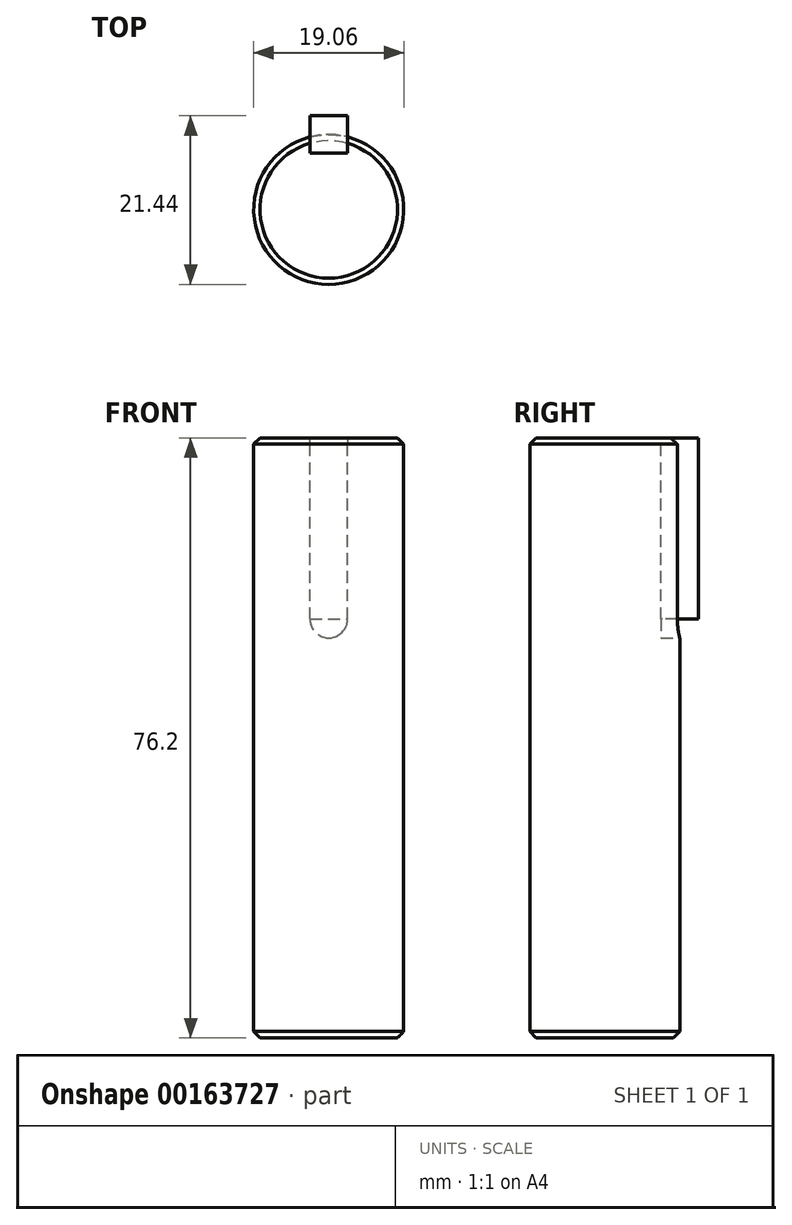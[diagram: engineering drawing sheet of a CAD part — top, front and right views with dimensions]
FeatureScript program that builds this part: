
annotation { "Feature Type Name" : "Feature", "Feature Type Description" : "" }
export const myFeature = defineFeature(function(context is Context, id is Id, definition is map)
    precondition{}
    {
        {
            var Q0;
            Q0=qCreatedBy(makeId("Top.planeOp"),FACE);
            var sketch = newSketch(context, id + "F0", { "sketchPlane" : qUnion([Q0])});
            skCircle(sketch, "E0", {"center": v(0, 0) * mm, "radius": 9.53 * mm});
            skSolve(sketch);
        }
        {
            var Q0;
            Q0=makeQuery(id+"F0.imprint","IMPRINT",FACE,{"disambiguationData":[TD([[makeQuery(id+"F0.imprint","IMPRINT",EDGE,{"derivedFrom":sQuery(id+"F0.wireOp",EDGE,"E0")}),1.0]])]});
            extrude(context, id + "F1", {"entities" : qUnion([Q0]), "depth" : 76.2 * mm});
        }
        {
            var Q0;
            Q0=makeQuery(id+"F1.opExtrude","CAP_FACE",FACE,{"disambiguationData":[OSD([sQuery(id+"F0.wireOp",EDGE,"E0")])],"isStart":false});
            var sketch = newSketch(context, id + "F2", { "sketchPlane" : qUnion([Q0])});
            skLineSegment(sketch, "E1.bottom", {"start": v(-2.38, 11.9) * mm, "end": v(2.38, 11.9) * mm});
            skLineSegment(sketch, "E1.top", {"start": v(-2.38, 7.14) * mm, "end": v(2.38, 7.14) * mm});
            skLineSegment(sketch, "E1.left", {"start": v(-2.38, 11.9) * mm, "end": v(-2.38, 7.14) * mm});
            skLineSegment(sketch, "E1.right", {"start": v(2.38, 11.9) * mm, "end": v(2.38, 7.14) * mm});
            skPoint(sketch, "E1.middle", {"position": v(0, 9.53) * mm});
            skSolve(sketch);
        }
        {
            var Q0;
            {var subQ0=sQuery(id+"F2.wireOp",EDGE,"E1.top");Q0=makeQuery(id+"F2.imprint","IMPRINT",FACE,{"disambiguationData":[TD([[makeQuery(id+"F2.imprint","IMPRINT",EDGE,{"derivedFrom":subQ0}),1.0]])]});}
            extrude(context, id + "F3", {"entities" : qUnion([Q0]), "operationType" : NewBodyOperationType.REMOVE, "oppositeDirection" : true, "depth" : 25.4 * mm});
        }
        {
            var Q0;
            Q0=makeQuery(id+"F3.boolean.opBoolean","COPY",EDGE,{"derivedFrom":makeQuery(id+"F3.opExtrude","CAP_EDGE",EDGE,{"disambiguationData":[OSD([sQuery(id+"F2.wireOp",EDGE,"E1.right")])],"isStart":false})});
            var Q1;
            Q1=makeQuery(id+"F3.boolean.opBoolean","COPY",EDGE,{"derivedFrom":makeQuery(id+"F3.opExtrude","CAP_EDGE",EDGE,{"disambiguationData":[OSD([sQuery(id+"F2.wireOp",EDGE,"E1.left")])],"isStart":false})});
            fillet(context, id + "F4", {"entities" : qUnion([Q0, Q1]), "radius" : 2.38 * mm, "tangentPropagation" : true, "allowEdgeOverflow" : false});
        }
        {
            var Q0;
            Q0=makeQuery(id+"F3.boolean.opBoolean","COPY",FACE,{"derivedFrom":makeQuery(id+"F3.opExtrude","SWEPT_FACE",FACE,{"disambiguationData":[OSD([sQuery(id+"F2.wireOp",EDGE,"E1.top")])]})});
            var sketch = newSketch(context, id + "F5", { "sketchPlane" : qUnion([Q0])});
            skLineSegment(sketch, "E2.bottom", {"start": v(2.38, 53.18) * mm, "end": v(-2.38, 53.18) * mm});
            skLineSegment(sketch, "E2.top", {"start": v(2.38, 76.2) * mm, "end": v(-2.38, 76.2) * mm});
            skLineSegment(sketch, "E2.left", {"start": v(2.38, 53.18) * mm, "end": v(2.38, 76.2) * mm});
            skLineSegment(sketch, "E2.right", {"start": v(-2.38, 53.18) * mm, "end": v(-2.38, 76.2) * mm});
            skSolve(sketch);
        }
        {
            var Q0;
            Q0=makeQuery(id+"F5.imprint","IMPRINT",FACE,{"disambiguationData":[TD([[makeQuery(id+"F5.imprint","IMPRINT",EDGE,{"derivedFrom":sQuery(id+"F5.wireOp",EDGE,"E2.bottom")}),-1.0]])]});
            extrude(context, id + "F6", {"entities" : qUnion([Q0]), "depth" : 4.76 * mm});
        }
        {
            var Q0;
            Q0=makeQuery(id+"F1.opExtrude","CAP_EDGE",EDGE,{"disambiguationData":[OSD([sQuery(id+"F0.wireOp",EDGE,"E0")])],"isStart":false});
            var Q1;
            Q1=makeQuery(id+"F1.opExtrude","CAP_EDGE",EDGE,{"disambiguationData":[OSD([sQuery(id+"F0.wireOp",EDGE,"E0")])],"isStart":true});
            chamfer(context, id + "F7", {"entities" : qUnion([Q0, Q1]), "width" : 0.8 * mm, "tangentPropagation" : true});
        }
    });
